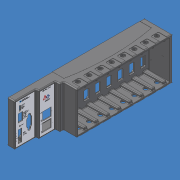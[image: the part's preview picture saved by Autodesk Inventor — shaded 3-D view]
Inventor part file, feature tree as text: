
AUTODESK INVENTOR PART (.ipt)
format: ipt  version: unknown  size: 1,508,864 bytes
history: native  units: mm (DEFAULTED — no unit token found)
features: sketch x25, extrude x19, pattern_linear x9, fillet x7, hole x4, mirror x2, other x2
ambient origin geometry x8: Origin, YZ Plane, XZ Plane, XY Plane, X Axis, Y Axis, Z Axis, Center Point
feature tree (68):
  extrude  "Extrusion1"  Depth=15.494mm
  extrude  "Extrusion2"  Depth=58.928mm
  extrude  "Extrusion3"  Depth=44.45mm
  extrude  "Extrusion4"  Depth=34.29mm
  extrude  "Extrusion5"  Depth=278.8412mm
  hole  "Hole2"  [1 undecoded]
  mirror  "Mirror2"
  pattern_linear  "Rectangular Pattern1"  Count1=2 Spacing1=93.0148mm
  pattern_linear  "Rectangular Pattern2"  Count1=2 Spacing1=140.589mm
  pattern_linear  "Rectangular Pattern3"  Count1=2 Spacing1=235.077mm
  pattern_linear  "Rectangular Pattern5"  Count1=2 Spacing1=81.534mm
  hole  "Hole3"  [1 undecoded]
  extrude  "Extrusion6"  Depth=11.1125mm
  extrude  "Extrusion7"  Depth=15.875mm
  extrude  "Extrusion8"  Depth=9.8298mm
  pattern_linear  "Rectangular Pattern6"  Count1=2 Spacing1=165.1mm
  extrude  "Extrusion9"  Depth=20.32mm
  pattern_linear  "Rectangular Pattern7"  Spacing1=5.08mm  [1 undecoded]
  extrude  "Extrusion10"  Depth=6.35mm
  extrude  "Extrusion11"  Depth=1.905mm
  extrude  "Extrusion12"  Depth=3.175mm TaperAngle=0.0deg
  extrude  "Extrusion13"  Depth=80.0mm
  extrude  "Extrusion14"  Depth=83.058mm
  pattern_linear  "Rectangular Pattern8"  Spacing1=39.624mm  [1 undecoded]
  extrude  "Extrusion15"  Depth=0.508mm TaperAngle=0.0deg
  fillet  "Fillet1"  Radius=83.058mm
  fillet  "Fillet4"  Radius=30.48mm
  extrude  "Extrusion19"  Depth=0.508mm TaperAngle=0.0deg
  extrude  "Extrusion16"  Depth=39.37mm
  extrude  "Extrusion17"  Depth=41.275mm
  fillet  "Fillet2"  Radius=6.35mm
  hole  "Hole4"  [1 undecoded]
  pattern_linear  "Rectangular Pattern9"  Spacing1=9.525mm  [1 undecoded]
  mirror  "Mirror4"
  extrude  "Extrusion18"  Depth=18.034mm
  fillet  "Fillet3"  Radius=17.272mm
  pattern_linear  "Rectangular Pattern10"  Spacing1=5.715mm  [1 undecoded]
  hole  "Hole5"  [1 undecoded]
  fillet  "Fillet5"  Radius=20.0mm
  fillet  "Fillet7"  Radius=16.6116mm
  fillet  "Fillet8"  Radius=9.6774mm
  sketch  "Sketch1"  dims[d0=286.512mm d1=15.494mm]
  sketch  "Sketch2"  dims[d2=86.36mm d3=58.928mm]
  sketch  "Sketch3"  dims[d4=88.138mm d5=0.0mm d6=44.45mm]
  sketch  "Sketch4"  dims[d7=6.096mm d8=34.29mm]
  sketch  "Sketch6"  dims[d9=9.525mm d10=278.8412mm]
  sketch  "Sketch7"  dims[d11=80.4672mm d12=2.159mm d13=0.0mm]
  sketch  "Sketch8"  dims[d14=77.6732mm]
  sketch  "Sketch9"  dims[d15=276.0472mm]
  sketch  "Sketch10"  dims[d16=10.795mm d17=0.0mm]
  sketch  "Sketch11"  dims[d18=80.264mm]
  sketch  "Sketch12"  dims[d19=6.35mm]
  sketch  "Sketch13"  dims[d20=191.262mm]
  sketch  "Sketch14"  dims[d21=43.18mm d22=0.0mm]
  sketch  "Sketch15"  dims[d32=7.62mm]
  sketch  "Sketch16"  dims[d33=4.9149mm]
  sketch  "Sketch17"  dims[d34=11.6586mm]
  sketch  "Sketch18"  dims[d35=5.842mm d36=0.0mm]
  sketch  "Sketch19"  dims[d37=3.1242mm d38=12.7mm d39=9.525mm d40=6.35mm d41=14.3117mm d42=19.05mm d43=20.594885mm d44=20.0mm d46=93.0148mm d47=20.0mm d49=140.589mm d50=20.0mm d52=235.077mm d56=20.0mm d58=81.534mm]
  sketch  "Sketch20"  dims[d59=26.2636mm d60=59.055mm]
  sketch  "Sketch21"  dims[d61=165.1mm]
  sketch  "Sketch22"  dims[d62=5.334mm d63=12.7mm d64=9.525mm d65=6.35mm d66=14.3117mm d67=19.05mm d68=20.594885mm d69=11.1125mm]
  sketch  "Sketch23"  dims[d70=2.54mm d71=0.0mm d72=15.875mm]
  sketch  "Sketch25"  dims[d73=3.175mm d74=0.0mm d75=9.8298mm]
  sketch  "Sketch26"  dims[d76=3.175mm d77=0.0mm d78=20.0mm d80=165.1mm]
  sketch  "Sketch27"  dims[d81=11.0998mm d82=20.32mm d83=5.08mm d84=6.35mm d85=1.905mm d86=3.175mm d87=0.0mm d88=80.0mm d90=23.622mm d91=83.058mm d92=39.624mm d93=0.508mm d94=0.0mm d95=83.058mm d96=30.48mm d97=0.508mm d98=0.0mm d99=39.37mm d100=41.275mm d101=6.35mm d102=0.0mm d103=5.08mm d104=9.525mm d105=0.0mm d106=18.034mm d107=17.272mm d108=5.715mm d109=9.525mm d110=0.0mm d111=20.0mm d113=20.32mm d114=16.6116mm d115=9.6774mm d116=8.001mm d117=25.1968mm d119=4.953mm d120=4.572mm d121=5.08mm d122=24.13mm d123=11.176mm d124=10.16mm d125=7.493mm d126=3.048mm d127=9.525mm d128=0.0mm d129=1.524mm d130=3.175mm d131=8.89mm d132=35.306mm d133=10.668mm d134=182.88mm d135=25.4mm d136=24.638mm d137=0.381mm d138=0.0mm d139=19.05mm d140=15.875mm d141=0.762mm d142=0.0mm d143=2.54mm d144=13.97mm d145=8.89mm d146=12.7mm d147=9.525mm d148=6.35mm d149=14.3117mm d150=6.35mm d151=20.594885mm d152=80.0mm d154=23.622mm d155=9.525mm d156=4.572mm d157=0.254mm d158=40.64mm d159=0.0mm d161=0.349066mm d162=6.35mm d163=1.27mm d164=80.0mm d166=23.622mm d167=38.608mm d168=14.732mm d169=24.892mm d170=43.942mm d171=62.992mm d172=2.6416mm d173=12.7mm d174=9.525mm d175=6.35mm d176=14.3117mm d177=6.35mm d178=20.594885mm d179=6.096mm d180=31.242mm d181=25.4mm d182=17.272mm d183=3.048mm d195=3.175mm d196=20.32mm d197=17.453293mm d198=10.922mm d199=40.132mm d200=0.0mm d201=2.0066mm d203=1.27mm d204=0.508mm]
  other  "Image3"
  other  "Image4"
note: 8 required parameter values undecoded (feature->parameter linkage not recoverable at this tier; creation-order binding heuristic only, values carry confidence <= 0.55)
